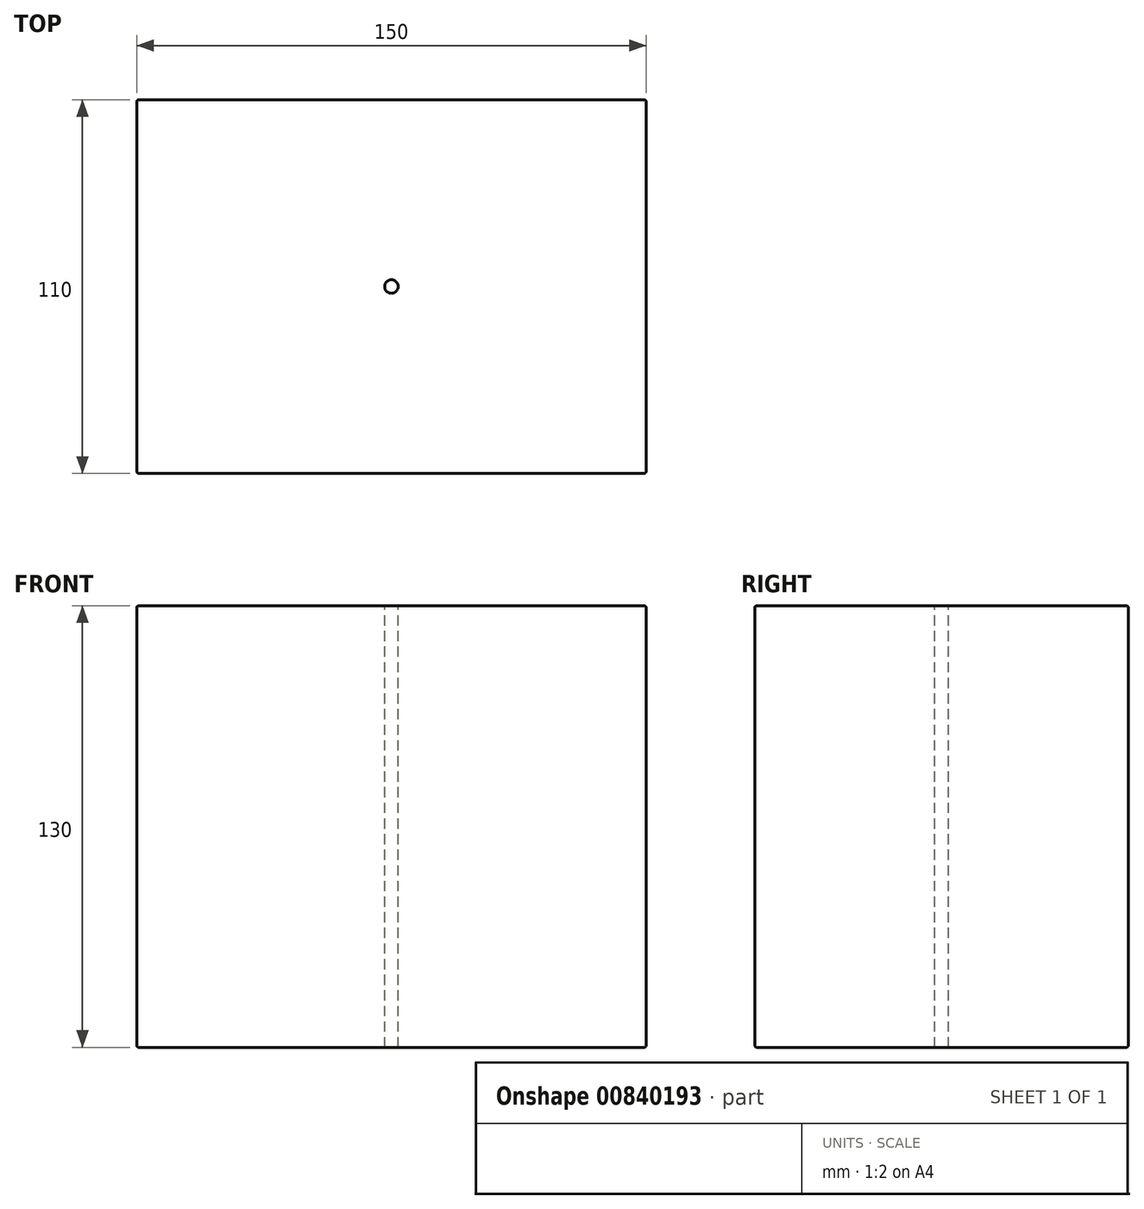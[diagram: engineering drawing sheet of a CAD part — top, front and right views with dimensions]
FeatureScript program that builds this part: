
annotation { "Feature Type Name" : "Feature", "Feature Type Description" : "" }
export const myFeature = defineFeature(function(context is Context, id is Id, definition is map)
    precondition{}
    {
        {
            var Q0;
            Q0=qCreatedBy(makeId("Top.planeOp"),FACE);
            var sketch = newSketch(context, id + "F0", { "sketchPlane" : qUnion([Q0])});
            skLineSegment(sketch, "E0.bottom", {"start": v(0, 110) * mm, "end": v(150, 110) * mm});
            skLineSegment(sketch, "E0.top", {"start": v(0, 0) * mm, "end": v(150, 0) * mm});
            skLineSegment(sketch, "E0.left", {"start": v(0, 110) * mm, "end": v(0, 0) * mm});
            skLineSegment(sketch, "E0.right", {"start": v(150, 110) * mm, "end": v(150, 0) * mm});
            skSolve(sketch);
        }
        {
            var Q0;
            Q0 = qSketchRegion(id + "F0", true);
            extrude(context, id + "F1", {"entities" : qUnion([Q0]), "depth" : 130 * mm, "offsetDistance" : 25 * mm});
        }
        {
            var Q0;
            Q0=makeQuery(id+"F1.opExtrude","CAP_FACE",FACE,{"disambiguationData":[OSD([sQuery(id+"F0.wireOp",EDGE,"E0.bottom"),sQuery(id+"F0.wireOp",EDGE,"E0.top"),sQuery(id+"F0.wireOp",EDGE,"E0.left"),sQuery(id+"F0.wireOp",EDGE,"E0.right")])],"isStart":false});
            var sketch = newSketch(context, id + "F2", { "sketchPlane" : qUnion([Q0])});
            skCircle(sketch, "E1", {"center": v(75, 55) * mm, "radius": 2 * mm});
            skPoint(sketch, "E1.centerSnap0", {"position": v(75, 110) * mm});
            skPoint(sketch, "E1.centerSnap1", {"position": v(0, 55) * mm});
            skSolve(sketch);
        }
        {
            var Q0;
            Q0 = qSketchRegion(id + "F2", true);
            extrude(context, id + "F3", {"entities" : qUnion([Q0]), "operationType" : NewBodyOperationType.REMOVE, "oppositeDirection" : true, "depth" : 130 * mm, "offsetDistance" : 25 * mm});
        }
        {
            var Q0;
            Q0=makeQuery(id+"F1.opExtrude","CAP_EDGE",EDGE,{"disambiguationData":[OSD([sQuery(id+"F0.wireOp",EDGE,"E0.bottom")])],"isStart":false});
            var Q1;
            Q1=makeQuery(id+"F1.opExtrude","CAP_EDGE",EDGE,{"disambiguationData":[OSD([sQuery(id+"F0.wireOp",EDGE,"E0.left")])],"isStart":false});
            var Q2;
            Q2=makeQuery(id+"F1.opExtrude","SWEPT_FACE",FACE,{"disambiguationData":[OSD([sQuery(id+"F0.wireOp",EDGE,"E0.bottom")])]});
            var Q3;
            Q3=makeQuery(id+"F1.opExtrude","SWEPT_FACE",FACE,{"disambiguationData":[OSD([sQuery(id+"F0.wireOp",EDGE,"E0.right")])]});
            var Q4;
            Q4=makeQuery(id+"F1.opExtrude","SWEPT_FACE",FACE,{"disambiguationData":[OSD([sQuery(id+"F0.wireOp",EDGE,"E0.top")])]});
            var Q5;
            Q5=makeQuery(id+"F1.opExtrude","SWEPT_FACE",FACE,{"disambiguationData":[OSD([sQuery(id+"F0.wireOp",EDGE,"E0.left")])]});
            fillet(context, id + "F4", {"entities" : qUnion([Q0, Q1, Q2, Q3, Q4, Q5]), "radius" : 0.6 * mm, "tangentPropagation" : true, "allowEdgeOverflow" : false});
        }
    });
